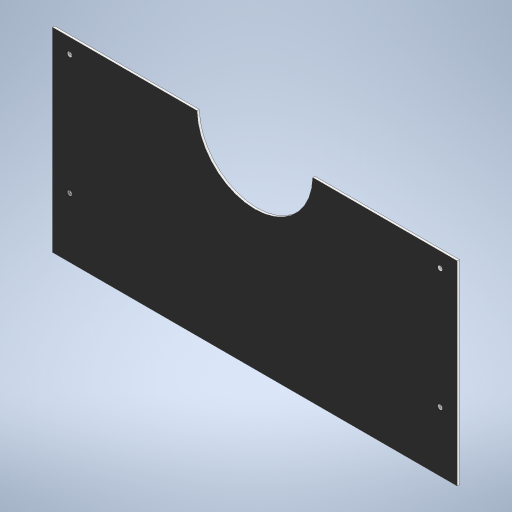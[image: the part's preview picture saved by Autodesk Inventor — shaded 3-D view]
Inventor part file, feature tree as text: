
AUTODESK INVENTOR PART (.ipt)
format: ipt  version: 2023 (Build 270158000, 158)  size: 235,008 bytes
history: native  units: mm
features: sketch x2, extrude x1, hole x1
ambient origin geometry x8: Origin, YZ Plane, XZ Plane, XY Plane, X Axis, Y Axis, Z Axis, Center Point
bodies: Solid1 (feature_tree)
feature tree (4):
  extrude  "Extrusion1"  Depth=3.0mm TaperAngle=0.0deg
  hole  "Hole1"  [1 undecoded]
  sketch  "Sketch1"  dims[d0=542.0mm d2=3.0mm d3=0.0mm]
  sketch  "Sketch2"  dims[d4=23.0mm d6=6.5mm d7=6.0mm d8=4.0mm d9=2.0mm d10=90.0deg d11=8.0mm d12=20.594885mm d13=20.0mm d14=261.0mm d15=542.0mm d16=20.0mm d18=161.0mm d19=20.0mm d21=496.0mm d24=155.0mm d25=263.0mm d26=261.0mm]
note: 1 required parameter value undecoded (feature->parameter linkage not recoverable at this tier; creation-order binding heuristic only, values carry confidence <= 0.55)
